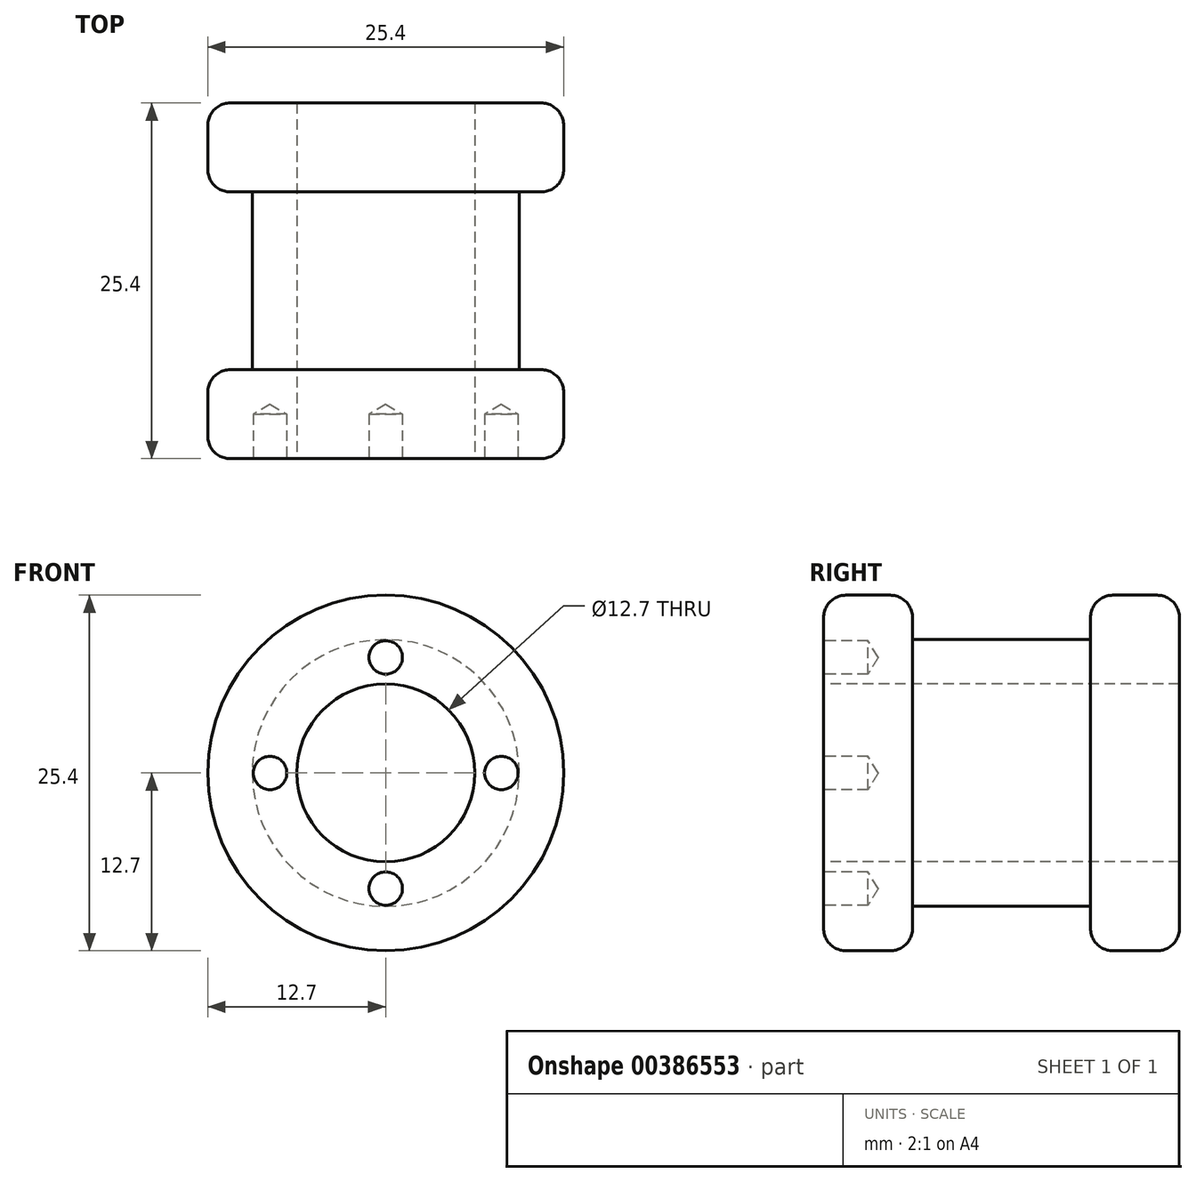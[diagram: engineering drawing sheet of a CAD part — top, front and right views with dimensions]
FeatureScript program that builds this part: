
annotation { "Feature Type Name" : "Feature", "Feature Type Description" : "" }
export const myFeature = defineFeature(function(context is Context, id is Id, definition is map)
    precondition{}
    {
        {
            var Q0;
            Q0=qCreatedBy(makeId("Front.planeOp"),FACE);
            var sketch = newSketch(context, id + "F0", { "sketchPlane" : qUnion([Q0])});
            skCircle(sketch, "E0", {"center": v(0, 0) * mm, "radius": 12.7 * mm});
            skSolve(sketch);
        }
        {
            var Q0;
            Q0 = qSketchRegion(id + "F0", true);
            extrude(context, id + "F1", {"entities" : qUnion([Q0]), "depth" : 6.35 * mm});
        }
        {
            var Q0;
            Q0=makeQuery(id+"F1.opExtrude","CAP_FACE",FACE,{"disambiguationData":[OSD([sQuery(id+"F0.wireOp",EDGE,"E0")])],"isStart":false});
            var sketch = newSketch(context, id + "F2", { "sketchPlane" : qUnion([Q0])});
            skCircle(sketch, "E1", {"center": v(0, 0) * mm, "radius": 9.53 * mm});
            skSolve(sketch);
        }
        {
            var Q0;
            Q0 = qSketchRegion(id + "F2", true);
            extrude(context, id + "F3", {"entities" : qUnion([Q0]), "operationType" : NewBodyOperationType.ADD, "depth" : 12.7 * mm});
        }
        {
            var Q0;
            Q0=makeQuery(id+"F3.opExtrude","CAP_FACE",FACE,{"disambiguationData":[OSD([sQuery(id+"F2.wireOp",EDGE,"E1")])],"isStart":false});
            var sketch = newSketch(context, id + "F4", { "sketchPlane" : qUnion([Q0])});
            skCircle(sketch, "E2", {"center": v(0, 0) * mm, "radius": 12.7 * mm});
            skSolve(sketch);
        }
        {
            var Q0;
            Q0 = qSketchRegion(id + "F4", true);
            extrude(context, id + "F5", {"entities" : qUnion([Q0]), "operationType" : NewBodyOperationType.ADD, "depth" : 6.35 * mm});
        }
        {
            var Q0;
            Q0=makeQuery(id+"F5.opExtrude","CAP_FACE",FACE,{"disambiguationData":[OSD([sQuery(id+"F4.wireOp",EDGE,"E2")])],"isStart":false});
            var sketch = newSketch(context, id + "F6", { "sketchPlane" : qUnion([Q0])});
            skCircle(sketch, "E3", {"center": v(0, 0) * mm, "radius": 6.35 * mm});
            skSolve(sketch);
        }
        {
            var Q0;
            Q0=sQuery(id+"F6.wireOp",VERTEX,"E3.center");
            var Q1;
            Q1=makeQuery(id+"F1.opExtrude","SWEPT_BODY",BODY,{"disambiguationData":[OSD([sQuery(id+"F0.wireOp",EDGE,"E0")])]});
            hole(context, id + "F7", {"style" : HoleStyle.SIMPLE, "endStyle" : HoleEndStyle.THROUGH, "holeDiameter" : 12.7 * mm, "isTappedThrough" : true, "tappedDepth" : 12.7 * mm, "tapClearance" : 3, "locations" : qUnion([Q0]), "scope" : qUnion([Q1])});
        }
        {
            var Q0;
            Q0=makeQuery(id+"F5.opExtrude","CAP_FACE",FACE,{"disambiguationData":[OSD([sQuery(id+"F4.wireOp",EDGE,"E2")])],"isStart":false});
            var sketch = newSketch(context, id + "F8", { "sketchPlane" : qUnion([Q0])});
            skPoint(sketch, "E4", {"position": v(0, 8.26) * mm});
            skPoint(sketch, "E5", {"position": v(-8.26, 0) * mm});
            skPoint(sketch, "E6", {"position": v(0, -8.26) * mm});
            skPoint(sketch, "E7", {"position": v(8.26, 0) * mm});
            skSolve(sketch);
        }
        {
            var Q0;
            Q0=sQuery(id+"F8.wireOp",VERTEX,"E4");
            var Q1;
            Q1=sQuery(id+"F8.wireOp",VERTEX,"E7");
            var Q2;
            Q2=sQuery(id+"F8.wireOp",VERTEX,"E6");
            var Q3;
            Q3=sQuery(id+"F8.wireOp",VERTEX,"E5");
            var Q4;
            Q4=makeQuery(id+"F1.opExtrude","SWEPT_BODY",BODY,{"disambiguationData":[OSD([sQuery(id+"F0.wireOp",EDGE,"E0")])]});
            hole(context, id + "F9", {"style" : HoleStyle.SIMPLE, "endStyle" : HoleEndStyle.BLIND, "holeDiameter" : 2.4 * mm, "holeDepth" : 3.17 * mm, "isTappedThrough" : true, "tappedDepth" : 12.7 * mm, "tapClearance" : 3, "locations" : qUnion([Q0, Q1, Q2, Q3]), "scope" : qUnion([Q4])});
        }
        {
            var Q0;
            Q0=makeQuery(id+"F1.opExtrude","CAP_EDGE",EDGE,{"disambiguationData":[OSD([sQuery(id+"F0.wireOp",EDGE,"E0")])],"isStart":true});
            var Q1;
            Q1=makeQuery(id+"F5.opExtrude","CAP_EDGE",EDGE,{"disambiguationData":[OSD([sQuery(id+"F4.wireOp",EDGE,"E2")])],"isStart":true});
            var Q2;
            Q2=makeQuery(id+"F5.opExtrude","CAP_EDGE",EDGE,{"disambiguationData":[OSD([sQuery(id+"F4.wireOp",EDGE,"E2")])],"isStart":false});
            var Q3;
            Q3=makeQuery(id+"F1.opExtrude","CAP_EDGE",EDGE,{"disambiguationData":[OSD([sQuery(id+"F0.wireOp",EDGE,"E0")])],"isStart":false});
            fillet(context, id + "F10", {"entities" : qUnion([Q0, Q1, Q2, Q3]), "radius" : 1.6 * mm, "tangentPropagation" : true, "allowEdgeOverflow" : false});
        }
    });
